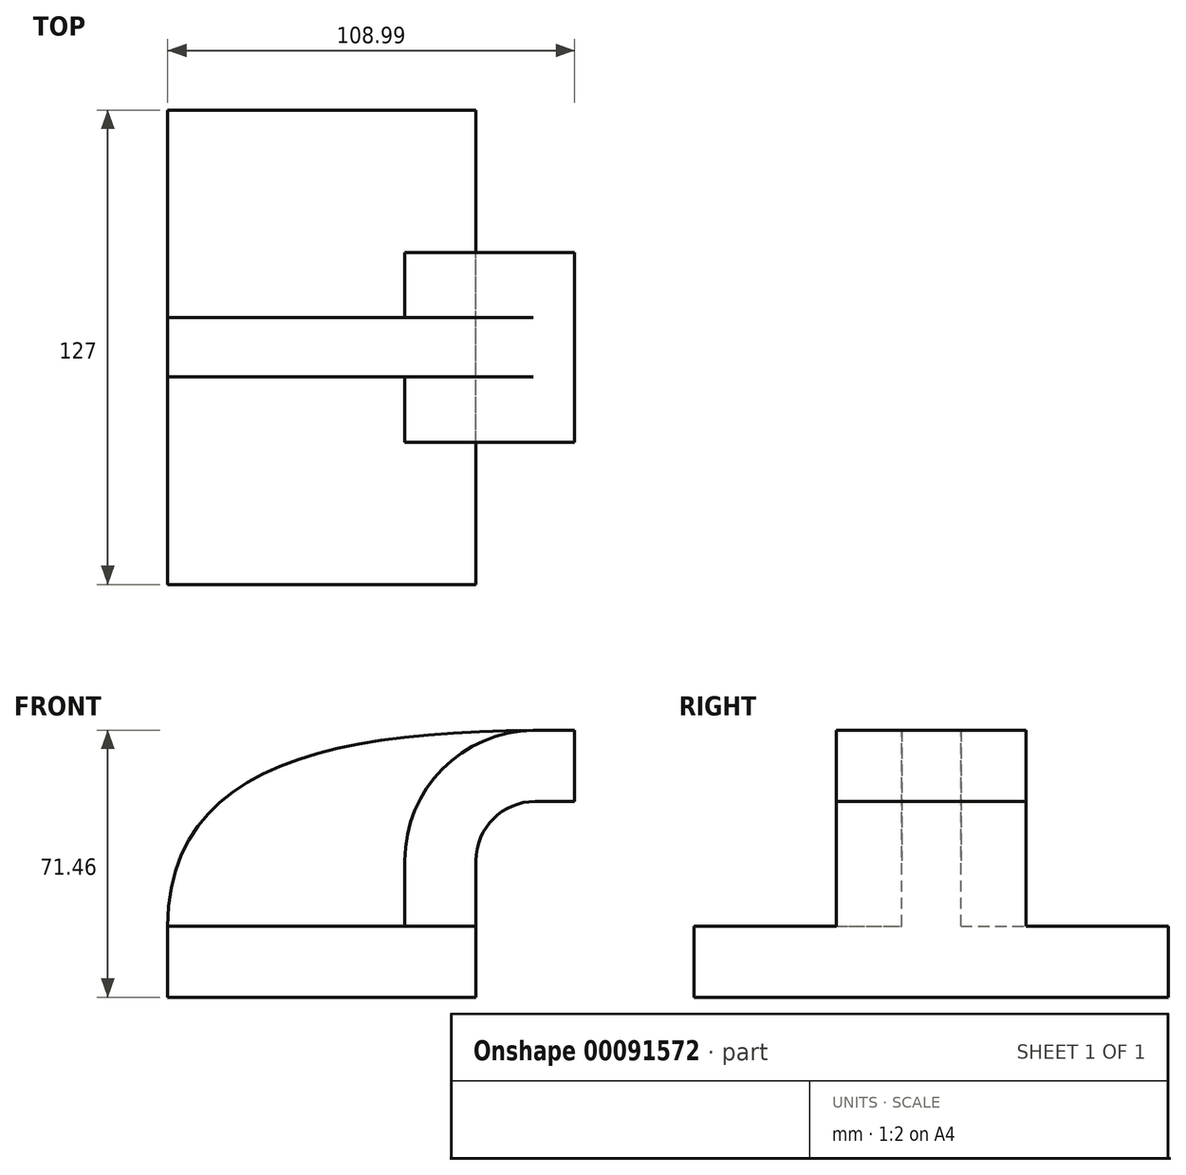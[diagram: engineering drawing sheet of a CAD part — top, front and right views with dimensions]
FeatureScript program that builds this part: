
annotation { "Feature Type Name" : "Feature", "Feature Type Description" : "" }
export const myFeature = defineFeature(function(context is Context, id is Id, definition is map)
    precondition{}
    {
        {
            var Q0;
            Q0=qCreatedBy(makeId("Front.planeOp"),FACE);
            var sketch = newSketch(context, id + "F0", { "sketchPlane" : qUnion([Q0])});
            skLineSegment(sketch, "E0.bottom", {"start": v(-41.28, 9.52) * mm, "end": v(41.28, 9.53) * mm});
            skLineSegment(sketch, "E0.top", {"start": v(-41.28, -9.53) * mm, "end": v(41.28, -9.53) * mm});
            skLineSegment(sketch, "E0.left", {"start": v(-41.28, 9.52) * mm, "end": v(-41.27, -9.53) * mm});
            skLineSegment(sketch, "E0.right", {"start": v(41.28, 9.53) * mm, "end": v(41.28, -9.52) * mm});
            skPoint(sketch, "E0.middle", {"position": v(0, 0) * mm});
            skLineSegment(sketch, "E1.bottom", {"start": v(67.71, 38.1) * mm, "end": v(118.51, 38.1) * mm});
            skLineSegment(sketch, "E1.top", {"start": v(67.71, 66.67) * mm, "end": v(118.51, 66.67) * mm});
            skLineSegment(sketch, "E1.left", {"start": v(67.71, 38.1) * mm, "end": v(67.71, 66.67) * mm});
            skLineSegment(sketch, "E1.right", {"start": v(118.51, 38.1) * mm, "end": v(118.51, 66.67) * mm});
            skPoint(sketch, "E1.middle", {"position": v(93.11, 52.39) * mm});
            skLineSegment(sketch, "E2", {"start": v(41.27, 9.53) * mm, "end": v(41.27, 27) * mm});
            skArc(sketch, "E3", {"start": v(41.27, 27) * mm, "mid": v(45.92, 38.23) * mm, "end": v(57.15, 42.88) * mm});
            skLineSegment(sketch, "E4", {"start": v(57.15, 42.88) * mm, "end": v(93.27, 42.88) * mm});
            skLineSegment(sketch, "E5.0", {"start": v(57.15, 61.93) * mm, "end": v(92.84, 61.93) * mm});
            skArc(sketch, "E5.1", {"start": v(22.22, 27) * mm, "mid": v(32.45, 51.7) * mm, "end": v(57.15, 61.93) * mm});
            skLineSegment(sketch, "E5.2", {"start": v(22.22, 9.53) * mm, "end": v(22.22, 27) * mm});
            skFitSpline(sketch, "E6", {"points": [v(-41.28, 9.52) * mm, v(57.15, 61.93) * mm], "startDerivative": vector(1.06, 126.02) * mm, "endDerivative": vector(171.45, 1.08) * mm});
            skLineSegment(sketch, "E7", {"start": v(92.84, 61.93) * mm, "end": v(93.27, 42.88) * mm});
            skSolve(sketch);
        }
        {
            var Q0;
            Q0=makeQuery(id+"F0.imprint","IMPRINT",FACE,{"disambiguationData":[TD([[makeQuery(id+"F0.imprint","IMPRINT",EDGE,{"derivedFrom":sQuery(id+"F0.wireOp",EDGE,"E0.top")}),1.0]])]});
            extrude(context, id + "F1", {"entities" : qUnion([Q0]), "endBound" : BoundingType.SYMMETRIC, "depth" : 127 * mm});
        }
        {
            var Q0;
            {var subQ1=sQuery(id+"F0.wireOp",EDGE,"E2");Q0=makeQuery(id+"F0.imprint","IMPRINT",FACE,{"disambiguationData":[TD([[makeQuery(id+"F0.imprint","IMPRINT",EDGE,{"derivedFrom":subQ1}),1.0]])]});}
            extrude(context, id + "F2", {"entities" : qUnion([Q0]), "operationType" : NewBodyOperationType.ADD, "endBound" : BoundingType.SYMMETRIC, "depth" : 50.8 * mm});
        }
        {
            var Q0;
            {var subQ3=sQuery(id+"F0.wireOp",EDGE,"E5.2");Q0=makeQuery(id+"F0.imprint","IMPRINT",FACE,{"disambiguationData":[TD([[makeQuery(id+"F0.imprint","IMPRINT",EDGE,{"derivedFrom":subQ3}),1.0]])]});}
            extrude(context, id + "F3", {"entities" : qUnion([Q0]), "operationType" : NewBodyOperationType.ADD, "endBound" : BoundingType.SYMMETRIC, "depth" : 15.88 * mm});
        }
    });
